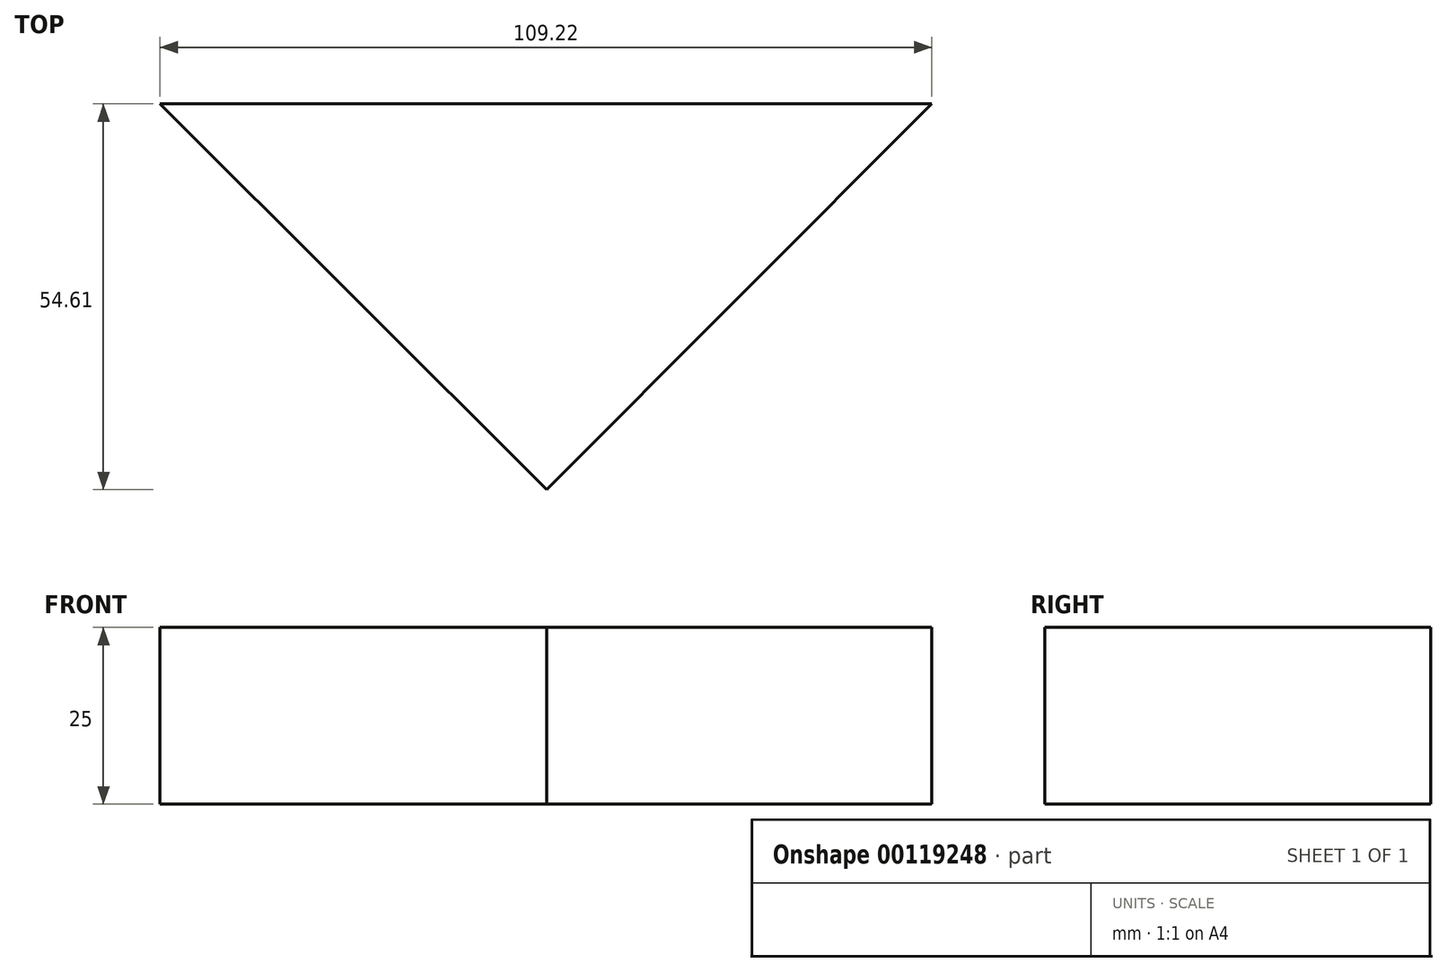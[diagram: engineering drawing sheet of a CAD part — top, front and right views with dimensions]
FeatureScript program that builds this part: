
annotation { "Feature Type Name" : "Feature", "Feature Type Description" : "" }
export const myFeature = defineFeature(function(context is Context, id is Id, definition is map)
    precondition{}
    {
        {
            var Q0;
            Q0=qCreatedBy(makeId("Top.planeOp"),FACE);
            var sketch = newSketch(context, id + "F0", { "sketchPlane" : qUnion([Q0])});
            skLineSegment(sketch, "E0", {"start": v(0, 0) * mm, "end": v(0, 54.32) * mm});
            skArc(sketch, "E1", {"start": v(-54.75, 0) * mm, "mid": v(-38.71, 38.71) * mm, "end": v(0, 54.75) * mm});
            skArc(sketch, "E2", {"start": v(54.47, 0) * mm, "mid": v(38.51, 38.51) * mm, "end": v(0, 54.47) * mm});
            skLineSegment(sketch, "E3", {"start": v(0, 0) * mm, "end": v(0, -54.6) * mm});
            skLineSegment(sketch, "E4", {"start": v(0, -54.6) * mm, "end": v(54.47, 0) * mm});
            skLineSegment(sketch, "E5", {"start": v(0, -54.6) * mm, "end": v(-54.75, 0) * mm});
            skLineSegment(sketch, "E6", {"start": v(-54.75, 0) * mm, "end": v(54.47, 0) * mm});
            skSolve(sketch);
        }
        {
            var Q0;
            {var subQ0=sQuery(id+"F0.wireOp",EDGE,"E3");Q0=makeQuery(id+"F0.imprint","IMPRINT",FACE,{"disambiguationData":[TD([[makeQuery(id+"F0.imprint","IMPRINT",EDGE,{"derivedFrom":subQ0}),1.0]])]});}
            var Q1;
            {var subQ0=sQuery(id+"F0.wireOp",EDGE,"E3");Q1=makeQuery(id+"F0.imprint","IMPRINT",FACE,{"disambiguationData":[TD([[makeQuery(id+"F0.imprint","IMPRINT",EDGE,{"derivedFrom":subQ0}),-1.0]])]});}
            extrude(context, id + "F1", {"entities" : qUnion([Q0, Q1]), "depth" : 25 * mm});
        }
    });
